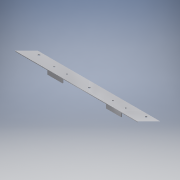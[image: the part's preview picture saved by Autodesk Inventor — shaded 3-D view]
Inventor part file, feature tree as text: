
AUTODESK INVENTOR PART (.ipt)
format: ipt  version: 2016 (Build 200138000, 138)  size: 193,024 bytes
history: native  units: in
note: dims shown in document units (in); Inventor stores cm internally (conversion verified against a paired STEP export)
features: extrude x5, sketch x5
ambient origin geometry x8: Origin, YZ Plane, XZ Plane, XY Plane, X Axis, Y Axis, Z Axis, Center Point
bodies: Solid1 (feature_tree)
feature tree (10):
  extrude  "Extrusion1"  Depth=2.0in
  extrude  "Extrusion2"  Depth=0.125in
  extrude  "Extrusion3"  Depth=15.0in
  extrude  "Extrusion4"  Depth=0.125in
  extrude  "Extrusion5"  Depth=2.25in
  sketch  "Sketch1"  dims[d0=30.0in d1=2.0in]
  sketch  "Sketch2"  dims[d2=0.125in d3=0.0in d4=0.375in]
  sketch  "Sketch3"  dims[d5=1.125in d6=15.0in]
  sketch  "Sketch4"  dims[d7=0.125in d8=0.0in d9=0.375in]
  sketch  "Sketch5"  dims[d10=1.5in d12=0.375in d13=1.5in d15=30.0in d16=0.875in d17=0.125in d18=0.0in d19=30.0in d20=0.875in d21=0.125in d22=0.0in d23=6.5in d24=1.25in d25=8.5in d26=3.0in d27=6.5in d28=1.25in d29=2.25in d30=0.0in d31=10.5in d32=10.5in d33=0.2656in d34=8.0in d35=1.0in d36=0.2656in d37=1.0in d38=10.5in d39=0.2656in d40=0.2656in d41=1.0in d42=1.0in d43=8.0in d44=10.5in]
